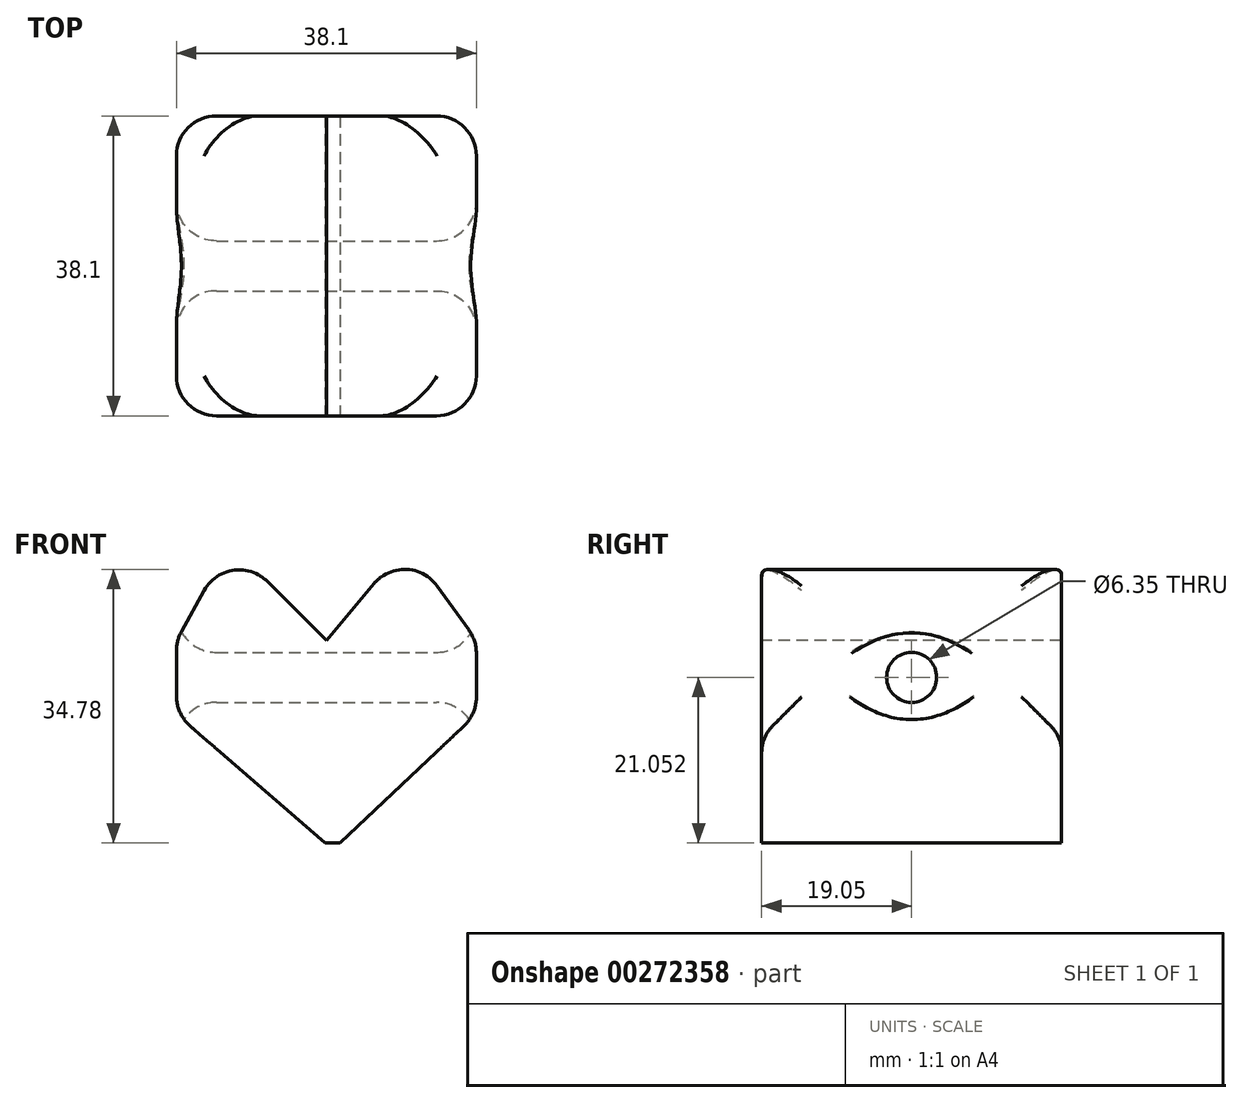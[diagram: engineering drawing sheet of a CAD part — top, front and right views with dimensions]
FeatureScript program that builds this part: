
annotation { "Feature Type Name" : "Feature", "Feature Type Description" : "" }
export const myFeature = defineFeature(function(context is Context, id is Id, definition is map)
    precondition{}
    {
        {
            var Q0;
            Q0=qCreatedBy(makeId("Front.planeOp"),FACE);
            var sketch = newSketch(context, id + "F0", { "sketchPlane" : qUnion([Q0])});
            skLineSegment(sketch, "E0", {"start": v(0, 0) * mm, "end": v(0, 38.1) * mm});
            skLineSegment(sketch, "E1", {"start": v(0, 38.1) * mm, "end": v(38.1, 38.1) * mm});
            skLineSegment(sketch, "E2", {"start": v(38.1, 38.1) * mm, "end": v(38.1, 0) * mm});
            skLineSegment(sketch, "E3", {"start": v(38.1, 0) * mm, "end": v(-0.4, 0.27) * mm});
            skSolve(sketch);
        }
        {
            var Q0;
            Q0 = qSketchRegion(id + "F0", true);
            extrude(context, id + "F1", {"entities" : qUnion([Q0]), "depth" : 38.1 * mm});
        }
        {
            var Q0;
            Q0=makeQuery(id+"F1.opExtrude","CAP_FACE",FACE,{"disambiguationData":[OSD([sQuery(id+"F0.wireOp",EDGE,"E0"),sQuery(id+"F0.wireOp",EDGE,"E1"),sQuery(id+"F0.wireOp",EDGE,"E2"),sQuery(id+"F0.wireOp",EDGE,"E3")])],"isStart":false});
            var sketch = newSketch(context, id + "F2", { "sketchPlane" : qUnion([Q0])});
            skLineSegment(sketch, "E4", {"start": v(19.05, 0) * mm, "end": v(0, 16.5) * mm});
            skPoint(sketch, "E4.startSnap0", {"position": v(19.05, 0.13) * mm});
            skLineSegment(sketch, "E5", {"start": v(0, 16.5) * mm, "end": v(0, 25.85) * mm});
            skLineSegment(sketch, "E6", {"start": v(0, 25.85) * mm, "end": v(6.78, 38.1) * mm});
            skLineSegment(sketch, "E7", {"start": v(6.78, 38.1) * mm, "end": v(19.05, 25.85) * mm});
            skPoint(sketch, "E7.endSnap0", {"position": v(19.05, 38.1) * mm});
            skLineSegment(sketch, "E8", {"start": v(19.05, 25.85) * mm, "end": v(29.29, 38.1) * mm});
            skLineSegment(sketch, "E9", {"start": v(29.29, 38.1) * mm, "end": v(38.1, 25.85) * mm});
            skLineSegment(sketch, "E10", {"start": v(38.1, 25.85) * mm, "end": v(38.1, 16.5) * mm});
            skLineSegment(sketch, "E11", {"start": v(38.1, 16.5) * mm, "end": v(20.8, 0.12) * mm});
            skSolve(sketch);
        }
        {
            var Q0;
            {var subQ0=sQuery(id+"F2.wireOp",EDGE,"E7");Q0=makeQuery(id+"F2.imprint","IMPRINT",FACE,{"disambiguationData":[TD([[makeQuery(id+"F2.imprint","IMPRINT",EDGE,{"derivedFrom":subQ0}),1.0]])]});}
            var Q1;
            {var subQ0=sQuery(id+"F2.wireOp",EDGE,"E6");Q1=makeQuery(id+"F2.imprint","IMPRINT",FACE,{"disambiguationData":[TD([[makeQuery(id+"F2.imprint","IMPRINT",EDGE,{"derivedFrom":subQ0}),1.0]])]});}
            var Q2;
            {var subQ0=sQuery(id+"F2.wireOp",EDGE,"E9");Q2=makeQuery(id+"F2.imprint","IMPRINT",FACE,{"disambiguationData":[TD([[makeQuery(id+"F2.imprint","IMPRINT",EDGE,{"derivedFrom":subQ0}),1.0]])]});}
            var Q3;
            {var subQ1=makeQuery(id+"F1.opExtrude","CAP_EDGE",EDGE,{"disambiguationData":[OSD([sQuery(id+"F0.wireOp",EDGE,"E0")])],"isStart":false});var subQ3=makeQuery(id+"F1.opExtrude","CAP_EDGE",EDGE,{"disambiguationData":[OSD([sQuery(id+"F0.wireOp",EDGE,"E3")])],"isStart":false});var subQ5=makeQuery(id+"F2.imprint","INTERSECT",VERTEX,{"derivedFrom":[subQ1,subQ3]});Q3=makeQuery(id+"F2.imprint","IMPRINT",FACE,{"disambiguationData":[TD([[makeQuery(id+"F2.imprint","IMPRINT",EDGE,{"disambiguationData":[TD([[subQ5,1.0]])],"derivedFrom":subQ3}),-1.0]])]});}
            var Q4;
            {var subQ0=sQuery(id+"F2.wireOp",EDGE,"E11");Q4=makeQuery(id+"F2.imprint","IMPRINT",FACE,{"disambiguationData":[TD([[makeQuery(id+"F2.imprint","IMPRINT",EDGE,{"derivedFrom":subQ0}),1.0]])]});}
            extrude(context, id + "F3", {"entities" : qUnion([Q0, Q1, Q2, Q3, Q4]), "operationType" : NewBodyOperationType.REMOVE, "oppositeDirection" : true, "depth" : 38.1 * mm});
        }
        {
            var Q0;
            Q0=makeQuery(id+"F1.opExtrude","SWEPT_FACE",FACE,{"disambiguationData":[OSD([sQuery(id+"F0.wireOp",EDGE,"E2")])]});
            var sketch = newSketch(context, id + "F4", { "sketchPlane" : qUnion([Q0])});
            skLineSegment(sketch, "E12", {"start": v(-19.05, 25.85) * mm, "end": v(-19.05, 16.5) * mm});
            skLineSegment(sketch, "E13", {"start": v(-38.1, 21.17) * mm, "end": v(0, 21.17) * mm});
            skCircle(sketch, "E14", {"center": v(-19.05, 21.17) * mm, "radius": 3.18 * mm});
            skSolve(sketch);
        }
        {
            var Q0;
            Q0=sQuery(id+"F4.wireOp",VERTEX,"E14.center");
            var Q1;
            Q1=makeQuery(id+"F1.opExtrude","SWEPT_BODY",BODY,{"disambiguationData":[OSD([sQuery(id+"F0.wireOp",EDGE,"E0"),sQuery(id+"F0.wireOp",EDGE,"E1"),sQuery(id+"F0.wireOp",EDGE,"E2"),sQuery(id+"F0.wireOp",EDGE,"E3")])]});
            hole(context, id + "F5", {"style" : HoleStyle.SIMPLE, "endStyle" : HoleEndStyle.THROUGH, "holeDiameter" : 6.35 * mm, "tappedDepth" : 12.7 * mm, "tapClearance" : 3, "locations" : qUnion([Q0]), "scope" : qUnion([Q1])});
        }
        {
            var Q0;
            Q0=makeQuery(id+"F1.opExtrude","SWEPT_FACE",FACE,{"disambiguationData":[OSD([sQuery(id+"F0.wireOp",EDGE,"E0")])]});
            var Q1;
            Q1=makeQuery(id+"F1.opExtrude","SWEPT_FACE",FACE,{"disambiguationData":[OSD([sQuery(id+"F0.wireOp",EDGE,"E2")])]});
            var Q2;
            Q2=makeQuery(id+"F3.boolean.opBoolean","COPY",FACE,{"derivedFrom":makeQuery(id+"F3.opExtrude","SWEPT_FACE",FACE,{"disambiguationData":[OSD([sQuery(id+"F2.wireOp",EDGE,"E6")])]})});
            var Q3;
            Q3=makeQuery(id+"F3.boolean.opBoolean","COPY",FACE,{"derivedFrom":makeQuery(id+"F3.opExtrude","SWEPT_FACE",FACE,{"disambiguationData":[OSD([sQuery(id+"F2.wireOp",EDGE,"E9")])]})});
            fillet(context, id + "F6", {"entities" : qUnion([Q0, Q1, Q2, Q3]), "radius" : 5.08 * mm, "tangentPropagation" : true, "allowEdgeOverflow" : false});
        }
    });
